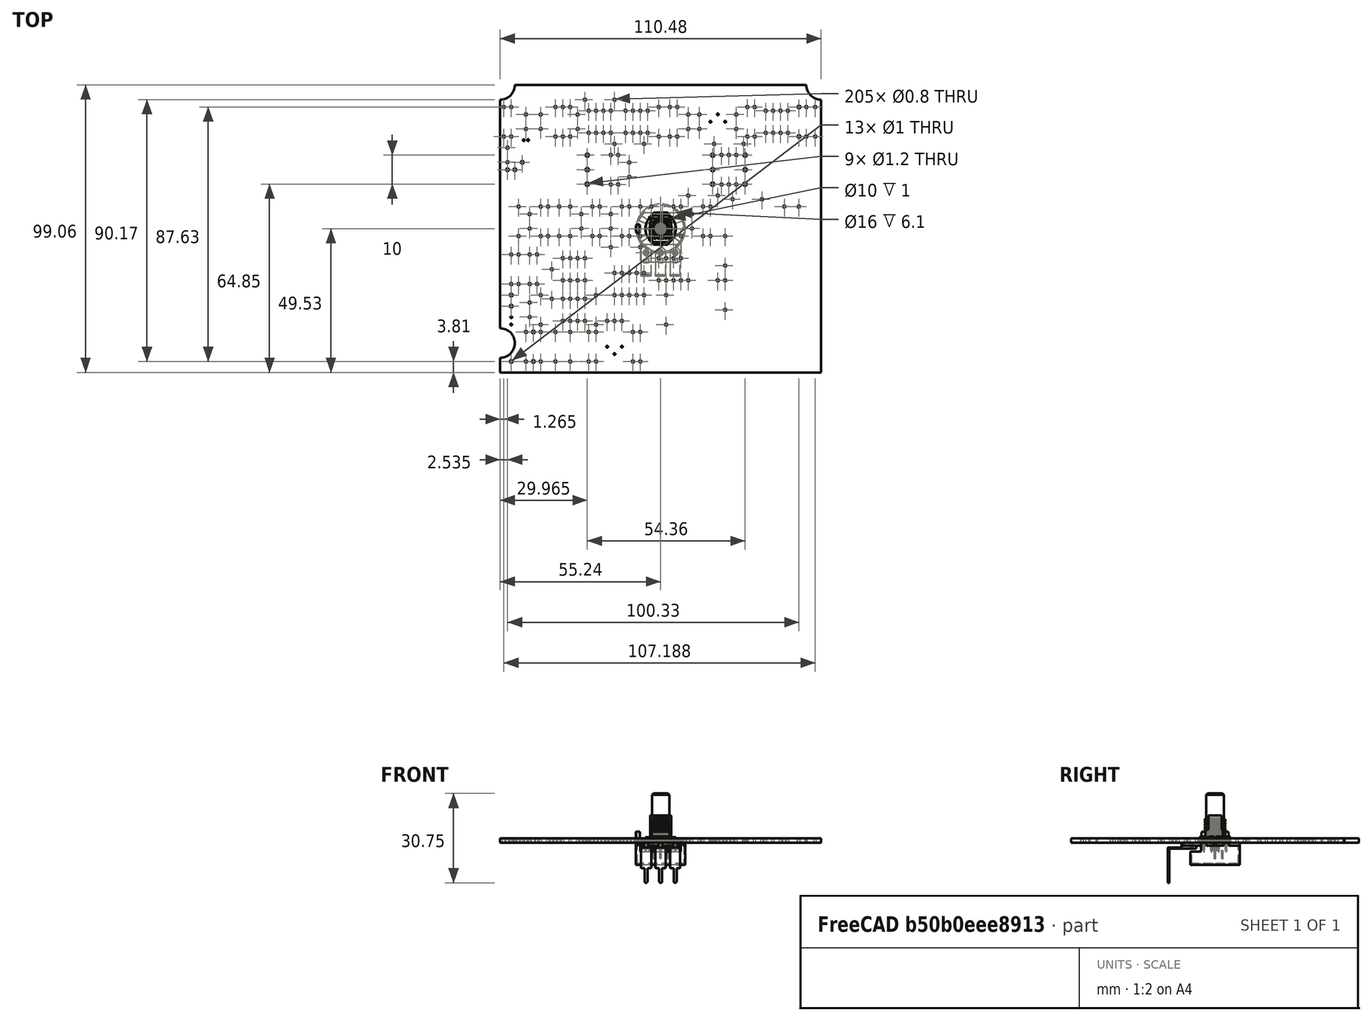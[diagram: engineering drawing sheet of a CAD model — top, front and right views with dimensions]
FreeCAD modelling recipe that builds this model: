
FCSTD DOCUMENT  (FreeCAD 0.19R17089 +1543 (Git))
Label: PRJ-003-#000-000 - Lid Assy
License: All rights reserved
LicenseURL: http://en.wikipedia.org/wiki/All_rights_reserved
objects: App::Link×58, Part::Feature×37, App::LinkGroup×33, Part::FeaturePython×26, App::FeaturePython×7
note: 62 computed .brp shape members not serialized (recipe doc carries the construction recipe); baked Part::Feature solids carry a one-line shape summary decoded from their .brp
EXTERNAL_REF file=../#700-000 - Enclosure/#710-000 - 1590DD.FCStd obj=Cut
EXTERNAL_REF file=../#700-000 - Enclosure/#710-000 - 1590DD.FCStd obj=Part__Feature

FEATURE [App::Link] Link
  LinkPlacement = pos=(6.90814,-46.0555,79.4472) rot=(0,1,0;3.14159rad)
  LinkedObject = -> <external ../#700-000 - Enclosure/#710-000 - 1590DD.FCStd>#Cut
  Placement = pos=(6.90814,-46.0555,79.4472) rot=(0,1,0;3.14159rad)
FEATURE [Part::Feature] Solid  label="SOLID"
  shape: bbox 10.96 x 2.55 x 5.125 mm, 27 faces (baked)
FEATURE [App::LinkGroup] LinkGroup  label="R_CC25_P10.16_H_27k"
  ElementList = -> [Solid]
  LinkMode = 0
  Placement = pos=(53.213,36.83,1.65) rot=(0,0,1;1.5708rad)
FEATURE [Part::Feature] Solid001  label="SOLID001"
  shape: bbox 10.96 x 2.55 x 5.125 mm, 27 faces (baked)
FEATURE [App::LinkGroup] LinkGroup001  label="R_CC25_P10.16_H_100k"
  ElementList = -> [Solid001]
  LinkMode = 0
  Placement = pos=(50.165,36.83,1.65) rot=(0,0,-1;1.5708rad)
FEATURE [Part::Feature] Solid002  label="SOLID002"
  shape: bbox 10.96 x 2.55 x 5.125 mm, 27 faces (baked)
FEATURE [App::LinkGroup] LinkGroup002  label="R_CC25_P10.16_H_220R"
  ElementList = -> [Solid002]
  LinkMode = 0
  Placement = pos=(-22.225,-40.64,1.65) rot=(0,0,-1;1.5708rad)
FEATURE [Part::Feature] Solid003  label="SOLID003"
  shape: bbox 10.96 x 2.55 x 5.125 mm, 27 faces (baked)
FEATURE [App::LinkGroup] LinkGroup003  label="R_CC25_P10.16_H_68k"
  ElementList = -> [Solid003]
  LinkMode = 0
  Placement = pos=(-41.275,-40.64,1.65) rot=(0,0,-1;1.5708rad)
FEATURE [Part::Feature] Solid004  label="SOLID004"
  shape: bbox 10.96 x 2.55 x 5.125 mm, 27 faces (baked)
FEATURE [App::LinkGroup] LinkGroup004  label="R_CC25_P10.16_H_220k"
  ElementList = -> [Solid004]
  LinkMode = 0
  Placement = pos=(-24.765,-40.64,1.65) rot=(0,0,-1;1.5708rad)
FEATURE [Part::Feature] Solid005  label="SOLID005"
  shape: bbox 10.96 x 2.55 x 5.125 mm, 27 faces (baked)
FEATURE [App::LinkGroup] LinkGroup005  label="R_CC25_P10.16_H_10k"
  ElementList = -> [Solid005]
  LinkMode = 0
  Placement = pos=(-36.195,-40.64,1.65) rot=(0,0,-1;1.5708rad)
FEATURE [Part::Feature] Solid006  label="SOLID006"
  shape: bbox 10.96 x 2.55 x 5.125 mm, 27 faces (baked)
FEATURE [App::LinkGroup] LinkGroup006  label="R_CC25_P10.16_H_3.3k"
  ElementList = -> [Solid006]
  LinkMode = 0
  Placement = pos=(-31.115,-40.64,1.65) rot=(0,0,-1;1.5708rad)
FEATURE [Part::Feature] Solid007  label="SOLID007"
  shape: bbox 10.96 x 2.55 x 5.125 mm, 27 faces (baked)
FEATURE [App::LinkGroup] LinkGroup007  label="R_CC25_P10.16_H_47k"
  ElementList = -> [Solid007]
  LinkMode = 0
  Placement = pos=(-9.525,-40.64,1.65) rot=(0,0,-1;1.5708rad)
FEATURE [Part::Feature] Solid008  label="SOLID008"
  shape: bbox 10.96 x 2.55 x 5.125 mm, 27 faces (baked)
FEATURE [App::LinkGroup] LinkGroup008  label="R_CC25_P10.16_H_82k"
  ElementList = -> [Solid008]
  LinkMode = 0
  Placement = pos=(-6.985,-40.64,1.65) rot=(0,0,-1;1.5708rad)
FEATURE [Part::Feature] Solid009  label="SOLID009"
  shape: bbox 10.96 x 2.55 x 5.125 mm, 27 faces (baked)
FEATURE [App::LinkGroup] LinkGroup009  label="R_CC25_P10.16_H_560R"
  ElementList = -> [Solid009]
  LinkMode = 0
  Placement = pos=(20.955,20.32,1.65) rot=(0,0,-1;1.5708rad)
FEATURE [App::Link] Link001  label="R_CC25_P10.16_H_27k001"
  LinkPlacement = pos=(26.035,20.32,1.65) rot=(0,0,-1;1.5708rad)
  LinkedObject = -> LinkGroup
  Placement = pos=(26.035,20.32,1.65) rot=(0,0,-1;1.5708rad)
FEATURE [Part::Feature] Solid010  label="SOLID010"
  shape: bbox 10.96 x 2.55 x 5.125 mm, 27 faces (baked)
FEATURE [App::LinkGroup] LinkGroup010  label="R_CC25_P10.16_H_82R"
  ElementList = -> [Solid010]
  LinkMode = 0
  Placement = pos=(23.495,20.32,1.65) rot=(0,0,-1;1.5708rad)
FEATURE [Part::Feature] Solid011  label="SOLID011"
  shape: bbox 10.96 x 2.55 x 5.125 mm, 27 faces (baked)
FEATURE [App::LinkGroup] LinkGroup011  label="R_CC25_P10.16_H_56k"
  ElementList = -> [Solid011]
  LinkMode = 0
  Placement = pos=(32.385,36.83,1.65) rot=(0,0,1;1.5708rad)
FEATURE [App::Link] Link002  label="R_CC25_P10.16_H_47k001"
  LinkPlacement = pos=(29.845,36.83,1.65) rot=(0,0,-1;1.5708rad)
  LinkedObject = -> LinkGroup007
  Placement = pos=(29.845,36.83,1.65) rot=(0,0,-1;1.5708rad)
FEATURE [App::Link] Link003  label="R_CC25_P10.16_H_560R001"
  LinkPlacement = pos=(-46.355,-40.64,1.65) rot=(0,0,-1;1.5708rad)
  LinkedObject = -> LinkGroup009
  Placement = pos=(-46.355,-40.64,1.65) rot=(0,0,-1;1.5708rad)
FEATURE [App::Link] Link004  label="R_CC25_P10.16_H_27k002"
  LinkPlacement = pos=(-41.275,-27.94,1.65) rot=(0,0,1;1.5708rad)
  LinkedObject = -> LinkGroup
  Placement = pos=(-41.275,-27.94,1.65) rot=(0,0,1;1.5708rad)
FEATURE [Part::Feature] Solid012  label="SOLID012"
  shape: bbox 10.96 x 2.55 x 5.125 mm, 27 faces (baked)
FEATURE [App::LinkGroup] LinkGroup012  label="R_CC25_P10.16_H_8.2k"
  ElementList = -> [Solid012]
  LinkMode = 0
  Placement = pos=(-48.895,-13.97,1.65) rot=(0,0,-1;1.5708rad)
FEATURE [App::Link] Link005  label="R_CC25_P10.16_H_10k001"
  LinkPlacement = pos=(-51.435,-13.97,1.65) rot=(0,0,1;1.5708rad)
  LinkedObject = -> LinkGroup005
  Placement = pos=(-51.435,-13.97,1.65) rot=(0,0,1;1.5708rad)
FEATURE [App::Link] Link006  label="R_CC25_P10.16_H_8.2k001"
  LinkPlacement = pos=(-45.085,-13.97,1.65) rot=(0,0,1;1.5708rad)
  LinkedObject = -> LinkGroup012
  Placement = pos=(-45.085,-13.97,1.65) rot=(0,0,1;1.5708rad)
FEATURE [App::Link] Link007  label="R_CC25_P10.16_H_10k002"
  LinkPlacement = pos=(-42.545,-13.97,1.65) rot=(0,0,1;1.5708rad)
  LinkedObject = -> LinkGroup005
  Placement = pos=(-42.545,-13.97,1.65) rot=(0,0,1;1.5708rad)
FEATURE [App::Link] Link008  label="R_CC25_P10.16_H_220k001"
  LinkPlacement = pos=(17.145,2.54,1.65) rot=(0,0,-1;1.5708rad)
  LinkedObject = -> LinkGroup004
  Placement = pos=(17.145,2.54,1.65) rot=(0,0,-1;1.5708rad)
FEATURE [Part::Feature] Solid013  label="SOLID013"
  shape: bbox 10.96 x 2.55 x 5.125 mm, 27 faces (baked)
FEATURE [App::LinkGroup] LinkGroup013  label="R_CC25_P10.16_H_4.7k"
  ElementList = -> [Solid013]
  LinkMode = 0
  Placement = pos=(5.715,36.83,1.65) rot=(0,0,1;1.5708rad)
FEATURE [App::Link] Link009  label="R_CC25_P10.16_H_4.7k001"
  LinkPlacement = pos=(3.175,36.83,1.65) rot=(0,0,-1;1.5708rad)
  LinkedObject = -> LinkGroup013
  Placement = pos=(3.175,36.83,1.65) rot=(0,0,-1;1.5708rad)
FEATURE [App::Link] Link010  label="R_CC25_P10.16_H_220k002"
  LinkPlacement = pos=(14.605,2.54,1.65) rot=(0,0,-1;1.5708rad)
  LinkedObject = -> LinkGroup004
  Placement = pos=(14.605,2.54,1.65) rot=(0,0,-1;1.5708rad)
FEATURE [App::Link] Link011  label="R_CC25_P10.16_H_4.7k002"
  LinkPlacement = pos=(-0.635,36.83,1.65) rot=(0,0,-1;1.5708rad)
  LinkedObject = -> LinkGroup013
  Placement = pos=(-0.635,36.83,1.65) rot=(0,0,-1;1.5708rad)
FEATURE [App::Link] Link012  label="R_CC25_P10.16_H_4.7k003"
  LinkPlacement = pos=(6.985,2.54,1.65) rot=(0,0,-1;1.5708rad)
  LinkedObject = -> LinkGroup013
  Placement = pos=(6.985,2.54,1.65) rot=(0,0,-1;1.5708rad)
FEATURE [App::Link] Link013  label="R_CC25_P10.16_H_220k003"
  LinkPlacement = pos=(4.445,2.54,1.65) rot=(0,0,1;1.5708rad)
  LinkedObject = -> LinkGroup004
  Placement = pos=(4.445,2.54,1.65) rot=(0,0,1;1.5708rad)
FEATURE [App::Link] Link014  label="R_CC25_P10.16_H_4.7k004"
  LinkPlacement = pos=(-3.175,2.54,1.65) rot=(0,0,-1;1.5708rad)
  LinkedObject = -> LinkGroup013
  Placement = pos=(-3.175,2.54,1.65) rot=(0,0,-1;1.5708rad)
FEATURE [App::Link] Link015  label="R_CC25_P10.16_H_4.7k005"
  LinkPlacement = pos=(-6.985,2.54,1.65) rot=(0,0,-1;1.5708rad)
  LinkedObject = -> LinkGroup013
  Placement = pos=(-6.985,2.54,1.65) rot=(0,0,-1;1.5708rad)
FEATURE [App::Link] Link016  label="R_CC25_P10.16_H_220k004"
  LinkPlacement = pos=(-13.335,2.54,1.65) rot=(0,0,1;1.5708rad)
  LinkedObject = -> LinkGroup004
  Placement = pos=(-13.335,2.54,1.65) rot=(0,0,1;1.5708rad)
FEATURE [App::Link] Link017  label="R_CC25_P10.16_H_4.7k006"
  LinkPlacement = pos=(-10.795,2.54,1.65) rot=(0,0,-1;1.5708rad)
  LinkedObject = -> LinkGroup013
  Placement = pos=(-10.795,2.54,1.65) rot=(0,0,-1;1.5708rad)
FEATURE [App::Link] Link018  label="R_CC25_P10.16_H_4.7k007"
  LinkPlacement = pos=(-20.955,2.54,1.65) rot=(0,0,-1;1.5708rad)
  LinkedObject = -> LinkGroup013
  Placement = pos=(-20.955,2.54,1.65) rot=(0,0,-1;1.5708rad)
FEATURE [App::Link] Link019  label="R_CC25_P10.16_H_220k005"
  LinkPlacement = pos=(-23.495,2.54,1.65) rot=(0,0,1;1.5708rad)
  LinkedObject = -> LinkGroup004
  Placement = pos=(-23.495,2.54,1.65) rot=(0,0,1;1.5708rad)
FEATURE [App::Link] Link020  label="R_CC25_P10.16_H_4.7k008"
  LinkPlacement = pos=(-31.115,2.54,1.65) rot=(0,0,-1;1.5708rad)
  LinkedObject = -> LinkGroup013
  Placement = pos=(-31.115,2.54,1.65) rot=(0,0,-1;1.5708rad)
FEATURE [App::Link] Link021  label="R_CC25_P10.16_H_4.7k009"
  LinkPlacement = pos=(-34.925,2.54,1.65) rot=(0,0,-1;1.5708rad)
  LinkedObject = -> LinkGroup013
  Placement = pos=(-34.925,2.54,1.65) rot=(0,0,-1;1.5708rad)
FEATURE [App::Link] Link022  label="R_CC25_P10.16_H_220k006"
  LinkPlacement = pos=(-48.895,2.54,1.65) rot=(0,0,1;1.5708rad)
  LinkedObject = -> LinkGroup004
  Placement = pos=(-48.895,2.54,1.65) rot=(0,0,1;1.5708rad)
FEATURE [App::Link] Link023  label="R_CC25_P10.16_H_4.7k010"
  LinkPlacement = pos=(-38.735,2.54,1.65) rot=(0,0,-1;1.5708rad)
  LinkedObject = -> LinkGroup013
  Placement = pos=(-38.735,2.54,1.65) rot=(0,0,-1;1.5708rad)
FEATURE [App::Link] Link024  label="R_CC25_P10.16_H_4.7k011"
  LinkPlacement = pos=(-41.275,2.54,1.65) rot=(0,0,1;1.5708rad)
  LinkedObject = -> LinkGroup013
  Placement = pos=(-41.275,2.54,1.65) rot=(0,0,1;1.5708rad)
FEATURE [App::Link] Link025  label="R_CC25_P10.16_H_8.2k002"
  LinkPlacement = pos=(-17.145,20.32,1.65) rot=(0,0,1;1.5708rad)
  LinkedObject = -> LinkGroup012
  Placement = pos=(-17.145,20.32,1.65) rot=(0,0,1;1.5708rad)
FEATURE [App::Link] Link026  label="R_CC25_P10.16_H_4.7k012"
  LinkPlacement = pos=(-14.605,20.32,1.65) rot=(0,0,-1;1.5708rad)
  LinkedObject = -> LinkGroup013
  Placement = pos=(-14.605,20.32,1.65) rot=(0,0,-1;1.5708rad)
FEATURE [App::Link] Link027  label="R_CC25_P10.16_H_4.7k013"
  LinkPlacement = pos=(-31.115,36.83,1.65) rot=(0,0,-1;1.5708rad)
  LinkedObject = -> LinkGroup013
  Placement = pos=(-31.115,36.83,1.65) rot=(0,0,-1;1.5708rad)
FEATURE [App::Link] Link028  label="R_CC25_P10.16_H_4.7k014"
  LinkPlacement = pos=(-33.655,36.83,1.65) rot=(0,0,-1;1.5708rad)
  LinkedObject = -> LinkGroup013
  Placement = pos=(-33.655,36.83,1.65) rot=(0,0,-1;1.5708rad)
FEATURE [Part::Feature] Solid014  label="SOLID014"
  shape: bbox 10.96 x 2.55 x 5.125 mm, 27 faces (baked)
FEATURE [App::LinkGroup] LinkGroup014  label="R_CC25_P10.16_H_390k"
  ElementList = -> [Solid014]
  LinkMode = 0
  Placement = pos=(-36.195,36.83,1.65) rot=(0,0,-1;1.5708rad)
FEATURE [Part::Feature] Solid015  label="SOLID015"
  shape: bbox 10.96 x 2.55 x 5.125 mm, 27 faces (baked)
FEATURE [App::LinkGroup] LinkGroup015  label="R_CC25_P10.16_H_3.9k"
  ElementList = -> [Solid015]
  LinkMode = 0
  Placement = pos=(-51.435,36.83,1.65) rot=(0,0,1;1.5708rad)
FEATURE [App::Link] Link029  label="R_CC25_P10.16_H_390k001"
  LinkPlacement = pos=(-53.975,36.83,1.65) rot=(0,0,-1;1.5708rad)
  LinkedObject = -> LinkGroup014
  Placement = pos=(-53.975,36.83,1.65) rot=(0,0,-1;1.5708rad)
FEATURE [Part::Feature] Solid016  label="SOLID016"
  shape: bbox 7.036 x 7.036 x 7.61 mm, 57 faces (baked)
FEATURE [App::LinkGroup] LinkGroup016  label="Nichicon_UMA_Straight_D6.5_H5_P2.5_d0.45_LL2.6"
  ElementList = -> [Solid016]
  LinkMode = 0
  Placement = pos=(-51.435,-31.75,1.65) rot=(0,0,1;3.14159rad)
FEATURE [Part::Feature] Solid017  label="SOLID017"
  shape: bbox 4.33 x 4.33 x 7.61 mm, 61 faces (baked)
FEATURE [App::LinkGroup] LinkGroup017  label="Nichicon_UMA_Straight_D4_H5_P1.5_d0.45_LL2.6"
  ElementList = -> [Solid017]
  LinkMode = 0
  Placement = pos=(-46.355,30.48,1.65) rot=(0,0,-1;1.5708rad)
FEATURE [Part::Feature] Solid018  label="SOLID018"
  shape: bbox 5.54 x 3.625 x 10.42 mm, 233 faces (baked)
FEATURE [App::LinkGroup] LinkGroup018  label="ON_Semi_2N3904TAR"
  ElementList = -> [Solid018]
  LinkMode = 0
  Placement = pos=(-15.875,-31.75,1.65) rot=(0,0,1;3.14159rad)
FEATURE [Part::Feature] Solid019  label="SOLID019"
  shape: bbox 6.706 x 7.036 x 10.16 mm, 550 faces (baked)
FEATURE [App::LinkGroup] LinkGroup019  label="Bourns_3362P-1-104"
  ElementList = -> [Solid019]
  LinkMode = 0
  Placement = pos=(-15.875,-40.64,1.65) rot=(0,0,1;3.14159rad)
FEATURE [App::Link] Link030  label="Bourns_3362P-1-105"
  LinkPlacement = pos=(19.685,36.83,1.65) rot=(0,0,1;0rad)
  LinkedObject = -> LinkGroup019
  Placement = pos=(19.685,36.83,1.65) rot=(0,0,1;0rad)
FEATURE [Part::Feature] Solid020  label="SOLID020"
  shape: bbox 10.96 x 2.5 x 5.1 mm, 11 faces (baked)
FEATURE [App::LinkGroup] LinkGroup020  label="R_CF25_P10.16_H"
  ElementList = -> [Solid020]
  LinkMode = 0
  Placement = pos=(22.225,-22.86,1.65) rot=(0,0,1;1.5708rad)
FEATURE [App::Link] Link031  label="R_CF25_P10.16_H001"
  LinkPlacement = pos=(29.845,10.16,1.65) rot=(0,0,1;3.14159rad)
  LinkedObject = -> LinkGroup020
  Placement = pos=(29.845,10.16,1.65) rot=(0,0,1;3.14159rad)
FEATURE [App::Link] Link032  label="R_CF25_P10.16_H002"
  LinkPlacement = pos=(14.605,11.43,1.65) rot=(0,0,1;3.14159rad)
  LinkedObject = -> LinkGroup020
  Placement = pos=(14.605,11.43,1.65) rot=(0,0,1;3.14159rad)
FEATURE [App::Link] Link033  label="R_CF25_P10.16_H003"
  LinkPlacement = pos=(22.225,-7.62,1.65) rot=(0,0,1;1.5708rad)
  LinkedObject = -> LinkGroup020
  Placement = pos=(22.225,-7.62,1.65) rot=(0,0,1;1.5708rad)
FEATURE [App::Link] Link034  label="R_CF25_P10.16_H004"
  LinkPlacement = pos=(14.605,-17.78,1.65) rot=(0,0,1;3.14159rad)
  LinkedObject = -> LinkGroup020
  Placement = pos=(14.605,-17.78,1.65) rot=(0,0,1;3.14159rad)
FEATURE [App::Link] Link035  label="R_CF25_P10.16_H005"
  LinkPlacement = pos=(1.905,-27.94,1.65) rot=(0,0,-1;1.5708rad)
  LinkedObject = -> LinkGroup020
  Placement = pos=(1.905,-27.94,1.65) rot=(0,0,-1;1.5708rad)
FEATURE [App::Link] Link036  label="R_CF25_P10.16_H006"
  LinkPlacement = pos=(-12.065,-6.35,1.65) rot=(0,0,1;3.14159rad)
  LinkedObject = -> LinkGroup020
  Placement = pos=(-12.065,-6.35,1.65) rot=(0,0,1;3.14159rad)
FEATURE [App::Link] Link037  label="R_CF25_P10.16_H007"
  LinkPlacement = pos=(-22.225,-27.94,1.65) rot=(0,0,1;1.5708rad)
  LinkedObject = -> LinkGroup020
  Placement = pos=(-22.225,-27.94,1.65) rot=(0,0,1;1.5708rad)
FEATURE [App::Link] Link038  label="R_CF25_P10.16_H008"
  LinkPlacement = pos=(-37.465,-19.05,1.65) rot=(0,0,1;1.5708rad)
  LinkedObject = -> LinkGroup020
  Placement = pos=(-37.465,-19.05,1.65) rot=(0,0,1;1.5708rad)
FEATURE [App::Link] Link039  label="R_CF25_P10.16_H009"
  LinkPlacement = pos=(23.495,29.21,1.65) rot=(0,0,1;0rad)
  LinkedObject = -> LinkGroup020
  Placement = pos=(23.495,29.21,1.65) rot=(0,0,1;0rad)
FEATURE [App::Link] Link040  label="R_CF25_P10.16_H010"
  LinkPlacement = pos=(-10.795,29.21,1.65) rot=(0,0,1;0rad)
  LinkedObject = -> LinkGroup020
  Placement = pos=(-10.795,29.21,1.65) rot=(0,0,1;0rad)
FEATURE [App::Link] Link041  label="R_CF25_P10.16_H011"
  LinkPlacement = pos=(-20.955,44.45,1.65) rot=(0,0,1;0rad)
  LinkedObject = -> LinkGroup020
  Placement = pos=(-20.955,44.45,1.65) rot=(0,0,1;0rad)
FEATURE [Part::Feature] Solid021  label="SOLID021"
  shape: bbox 7.87 x 9.59 x 7.1 mm, 280 faces (baked)
FEATURE [App::LinkGroup] LinkGroup021  label="Texas_Instruments_RC4558P"
  ElementList = -> [Solid021]
  LinkMode = 0
  Placement = pos=(-8.255,36.83,1.65) rot=(0,0,1;1.5708rad)
FEATURE [App::Link] Link042  label="Texas_Instruments_RC4558P001"
  LinkPlacement = pos=(3.175,-13.97,1.65) rot=(0,0,1;1.5708rad)
  LinkedObject = -> LinkGroup021
  Placement = pos=(3.175,-13.97,1.65) rot=(0,0,1;1.5708rad)
FEATURE [App::Link] Link043  label="Texas_Instruments_RC4558P002"
  LinkPlacement = pos=(-29.845,-13.97,1.65) rot=(0,0,1;1.5708rad)
  LinkedObject = -> LinkGroup021
  Placement = pos=(-29.845,-13.97,1.65) rot=(0,0,1;1.5708rad)
FEATURE [App::Link] Link044  label="Texas_Instruments_RC4558P003"
  LinkPlacement = pos=(40.005,36.83,1.65) rot=(0,0,1;1.5708rad)
  LinkedObject = -> LinkGroup021
  Placement = pos=(40.005,36.83,1.65) rot=(0,0,1;1.5708rad)
FEATURE [App::Link] Link045  label="Texas_Instruments_RC4558P004"
  LinkPlacement = pos=(-29.845,-27.94,1.65) rot=(0,0,1;1.5708rad)
  LinkedObject = -> LinkGroup021
  Placement = pos=(-29.845,-27.94,1.65) rot=(0,0,1;1.5708rad)
FEATURE [App::Link] Link046  label="Texas_Instruments_RC4558P005"
  LinkPlacement = pos=(-20.955,36.83,1.65) rot=(0,0,1;1.5708rad)
  LinkedObject = -> LinkGroup021
  Placement = pos=(-20.955,36.83,1.65) rot=(0,0,1;1.5708rad)
FEATURE [Part::Feature] Compound  label="COMPOUND"
  shape: bbox 13.5 x 9.75 x 13.95 mm, 243 faces, 3 solids (baked)
FEATURE [Part::Feature] Solid022  label="SOLID022"
  shape: bbox 6 x 6 x 8.5 mm, 4 faces (baked)
FEATURE [Part::Feature] Solid023  label="SOLID023"
  shape: bbox 7.238 x 7.394 x 6.855 mm, 40 faces (baked)
FEATURE [Part::Feature] Solid024  label="SOLID024"
  shape: bbox 16.98 x 20 x 1 mm, 46 faces (baked)
FEATURE [Part::Feature] Solid025  label="SOLID025"
  shape: bbox 17.02 x 17 x 11.4 mm, 108 faces (baked)
FEATURE [App::LinkGroup] LinkGroup022  label="RV16AF-41-15R"
  ElementList = -> [Compound,Solid022,Solid023,Solid024,Solid025]
  LinkMode = 0
  Placement = pos=(45.085,20.32,10.65) rot=(0,0,-1;1.5708rad)
FEATURE [App::Link] Link047  label="RV16AF-41-15R001"
  LinkPlacement = pos=(1.905,20.32,10.65) rot=(0,0,1;1.5708rad)
  LinkedObject = -> LinkGroup022
  Placement = pos=(1.905,20.32,10.65) rot=(0,0,1;1.5708rad)
FEATURE [App::Link] Link048  label="RV16AF-41-15R002"
  LinkPlacement = pos=(-41.275,20.32,10.65) rot=(0,0,1;1.5708rad)
  LinkedObject = -> LinkGroup022
  Placement = pos=(-41.275,20.32,10.65) rot=(0,0,1;1.5708rad)
FEATURE [Part::Feature] Solid026  label="SOLID026"
  shape: bbox 10.84 x 1.862 x 4.391 mm, 17 faces (baked)
FEATURE [App::LinkGroup] LinkGroup023  label="DO-35_P10.16"
  ElementList = -> [Solid026]
  LinkMode = 0
  Placement = pos=(-43.815,-40.64,1.65) rot=(0,0,1;1.5708rad)
FEATURE [App::Link] Link049  label="DO-35_P10.017"
  LinkPlacement = pos=(47.625,36.83,1.65) rot=(0,0,1;1.5708rad)
  LinkedObject = -> LinkGroup023
  Placement = pos=(47.625,36.83,1.65) rot=(0,0,1;1.5708rad)
FEATURE [Part::Feature] Solid027  label="SOLID027"
  shape: bbox 15.3 x 3.9 x 9.5 mm, 432 faces (baked)
FEATURE [App::LinkGroup] LinkGroup024  label="Wima_FKS2G016801B00KSSD"
  ElementList = -> [Solid027]
  LinkMode = 0
  Placement = pos=(45.085,7.62,1.65) rot=(0,0,1;3.14159rad)
FEATURE [Part::Feature] Solid028  label="SOLID028"
  shape: bbox 15.3 x 4.65 x 10.5 mm, 395 faces (baked)
FEATURE [App::LinkGroup] LinkGroup025  label="Wima_MKS2C034701C00KSSD"
  ElementList = -> [Solid028]
  LinkMode = 0
  Placement = pos=(26.035,36.83,1.65) rot=(0,0,-1;1.5708rad)
FEATURE [Part::Feature] Solid029  label="SOLID029"
  shape: bbox 15.3 x 6.15 x 8 mm, 402 faces (baked)
FEATURE [App::LinkGroup] LinkGroup026  label="Wima_FKP2J006801D00JSSD"
  ElementList = -> [Solid029]
  LinkMode = 0
  Placement = pos=(-45.085,-27.94,1.65) rot=(0,0,-1;1.5708rad)
FEATURE [App::Link] Link050  label="Wima_MKS2C034701C00KSSD001"
  LinkPlacement = pos=(13.335,36.83,1.65) rot=(0,0,1;1.5708rad)
  LinkedObject = -> LinkGroup025
  Placement = pos=(13.335,36.83,1.65) rot=(0,0,1;1.5708rad)
FEATURE [App::Link] Link051  label="Wima_FKS2G016801B00KSSD001"
  LinkPlacement = pos=(9.525,36.83,1.65) rot=(0,0,1;1.5708rad)
  LinkedObject = -> LinkGroup024
  Placement = pos=(9.525,36.83,1.65) rot=(0,0,1;1.5708rad)
FEATURE [App::Link] Link052  label="Wima_FKS2G016801B00KSSD002"
  LinkPlacement = pos=(10.795,2.54,1.65) rot=(0,0,1;1.5708rad)
  LinkedObject = -> LinkGroup024
  Placement = pos=(10.795,2.54,1.65) rot=(0,0,1;1.5708rad)
FEATURE [App::Link] Link053  label="Wima_FKS2G016801B00KSSD003"
  LinkPlacement = pos=(0.635,2.54,1.65) rot=(0,0,-1;1.5708rad)
  LinkedObject = -> LinkGroup024
  Placement = pos=(0.635,2.54,1.65) rot=(0,0,-1;1.5708rad)
FEATURE [App::Link] Link054  label="Wima_FKS2G016801B00KSSD004"
  LinkPlacement = pos=(-17.145,2.54,1.65) rot=(0,0,-1;1.5708rad)
  LinkedObject = -> LinkGroup024
  Placement = pos=(-17.145,2.54,1.65) rot=(0,0,-1;1.5708rad)
FEATURE [App::Link] Link055  label="Wima_FKS2G016801B00KSSD005"
  LinkPlacement = pos=(-27.305,2.54,1.65) rot=(0,0,-1;1.5708rad)
  LinkedObject = -> LinkGroup024
  Placement = pos=(-27.305,2.54,1.65) rot=(0,0,-1;1.5708rad)
FEATURE [App::Link] Link056  label="Wima_FKS2G016801B00KSSD006"
  LinkPlacement = pos=(-45.085,2.54,1.65) rot=(0,0,-1;1.5708rad)
  LinkedObject = -> LinkGroup024
  Placement = pos=(-45.085,2.54,1.65) rot=(0,0,-1;1.5708rad)
FEATURE [Part::Feature] Solid030  label="SOLID030"
  shape: bbox 15.3 x 3.15 x 8.5 mm, 428 faces (baked)
FEATURE [App::LinkGroup] LinkGroup027  label="Wima_FKS2G013301A00KSSD"
  ElementList = -> [Solid030]
  LinkMode = 0
  Placement = pos=(-10.795,20.32,1.65) rot=(0,0,-1;1.5708rad)
FEATURE [Part::Feature] Solid031  label="SOLID031"
  shape: bbox 15.3 x 3.15 x 8.5 mm, 398 faces (baked)
FEATURE [App::LinkGroup] LinkGroup028  label="Wima_FKS2G011001A00KSSD"
  ElementList = -> [Solid031]
  LinkMode = 0
  Placement = pos=(-28.575,36.83,1.65) rot=(0,0,1;1.5708rad)
FEATURE [Part::Feature] Solid032  label="SOLID032"
  shape: bbox 15.3 x 6.15 x 11.5 mm, 409 faces (baked)
FEATURE [App::LinkGroup] LinkGroup029  label="Wima_MKS2F031001E00KSSD"
  ElementList = -> [Solid032]
  LinkMode = 0
  Placement = pos=(-41.275,36.83,1.65) rot=(0,0,-1;1.5708rad)
FEATURE [Part::Feature] Solid033  label="SOLID033"
  shape: bbox 15.3 x 6.15 x 8 mm, 368 faces (baked)
FEATURE [App::LinkGroup] LinkGroup030  label="Wima_FKP2J001001D00JSSD"
  ElementList = -> [Solid033]
  LinkMode = 0
  Placement = pos=(-46.355,36.83,1.65) rot=(0,0,-1;1.5708rad)
FEATURE [Part::Feature] Solid034  label="SOLID034"
  shape: bbox 15.3 x 4.65 x 10.5 mm, 401 faces (baked)
FEATURE [App::LinkGroup] LinkGroup031  label="Wima_MKS2F024701C00KSSD"
  ElementList = -> [Solid034]
  LinkMode = 0
  Placement = pos=(-52.705,25.4,1.65) rot=(0,0,1;1.5708rad)
FEATURE [Part::Feature] Solid035  label="COMPOUND001"
  shape: bbox 110.5 x 99.06 x 1.6 mm, 248 faces (baked)
FEATURE [App::LinkGroup] LinkGroup032  label="Open CASCADE STEP translator 6.9 1"
  ElementList = -> [LinkGroup,LinkGroup001,LinkGroup002,LinkGroup003,LinkGroup004,LinkGroup005,LinkGroup006,LinkGroup007,LinkGroup008,LinkGroup009,Link001,LinkGroup010,LinkGroup011,Link002,Link003,Link004,LinkGroup012,Link005,Link006,Link007,Link008,LinkGroup013,Link009,Link010,Link011,Link012,Link013,Link014,Link015,Link016,Link017,Link018,Link019,Link020,Link021,Link022,Link023,Link024,Link025,Link026,Link027,+48 more]
  LinkMode = 0
  Placement = pos=(-14.3819,-68.9155,65.2972) rot=(0,0,-1;3.14159rad)
FEATURE [App::Link] Link057
  LinkPlacement = pos=(103.908,-46.0555,-38.6528) rot=(0,0,-1;1.5708rad)
  LinkedObject = -> <external ../#700-000 - Enclosure/#710-000 - 1590DD.FCStd>#Part__Feature
  Placement = pos=(103.908,-46.0555,-38.6528) rot=(0,0,-1;1.5708rad)
FEATURE [Part::FeaturePython] Parts  # WARN: FeaturePython — macro-defined, semantics opaque (R4)
  Group = -> [Link,LinkGroup032,Link057]
  GroupMode = 0
FEATURE [Part::FeaturePython] Assembly  # WARN: FeaturePython — macro-defined, semantics opaque (R4)
  AutoRelax = true
  BuildShape = 0
  Freeze = false
  Group = -> [Constraints,Elements,Parts]
  GroupMode = 1
  SolverType = 1
  Verbose = false
  _SolverType = 1
  _Version = 1
FEATURE [App::FeaturePython] Constraints  # WARN: FeaturePython — macro-defined, semantics opaque (R4)
  Group = -> [Constraint001,Constraint]
  GroupMode = 1
  _Version = 1
FEATURE [App::FeaturePython] Elements  # WARN: FeaturePython — macro-defined, semantics opaque (R4)
  Group = -> [_Element,_Element001,_Element002,_Element003,_Element004,_Element005,_Element006,_Element007,_Element008,_Element009,_Element010,_Element011,_Element012,_Element013,_Element014,_Element015,_Element016,_Element017,_Element018,_Element019,_Element020,_Element021,_Element022,_Element023]
  GroupMode = 1
FEATURE [Part::FeaturePython] _Element  # link proxy (typed FeaturePython)
  Detach = false
  LinkTransform = true
  LinkedObject = -> LinkGroup032 [LinkGroup022.Solid025.Face43]
  _Parent = -> Elements
FEATURE [Part::FeaturePython] _Element001  # link proxy (typed FeaturePython)
  Detach = false
  LinkTransform = true
  LinkedObject = -> Link [Face3]
  _Parent = -> Elements
FEATURE [Part::FeaturePython] _Element002  # link proxy (typed FeaturePython)
  Detach = false
  LinkTransform = true
  LinkedObject = -> Link [Edge108]
  _Parent = -> Elements
FEATURE [Part::FeaturePython] _Element003  # link proxy (typed FeaturePython)
  Detach = false
  LinkTransform = true
  LinkedObject = -> LinkGroup032 [LinkGroup022.Solid022.Face4]
  _Parent = -> Elements
FEATURE [Part::FeaturePython] _Element004  # link proxy (typed FeaturePython)
  Detach = false
  LinkTransform = true
  LinkedObject = -> LinkGroup032 [LinkGroup022.Solid022.Edge5]
  _Parent = -> Elements
FEATURE [Part::FeaturePython] _Element005  # link proxy (typed FeaturePython)
  Detach = false
  LinkTransform = true
  LinkedObject = -> Link [Edge110]
  _Parent = -> Elements
FEATURE [Part::FeaturePython] _Element006  # link proxy (typed FeaturePython)
  Detach = false
  LinkTransform = true
  LinkedObject = -> Link [Edge40]
  _Parent = -> Elements
FEATURE [Part::FeaturePython] _Element007  # link proxy (typed FeaturePython)
  Detach = false
  LinkTransform = true
  LinkedObject = -> LinkGroup032 [Link047.Solid022.Edge5]
  _Parent = -> Elements
FEATURE [Part::FeaturePython] _Element008  # link proxy (typed FeaturePython)
  Detach = false
  LinkTransform = true
  LinkedObject = -> Link [Edge38]
  _Parent = -> Elements
FEATURE [Part::FeaturePython] _Element009  # link proxy (typed FeaturePython)
  Detach = false
  LinkTransform = true
  LinkedObject = -> LinkGroup032 [Link048.Solid022.Edge5]
  _Parent = -> Elements
FEATURE [Part::FeaturePython] _Element010  # link proxy (typed FeaturePython)
  Detach = false
  LinkTransform = true
  LinkedObject = -> Link [Edge39]
  _Parent = -> Elements
FEATURE [Part::FeaturePython] _Element011  # link proxy (typed FeaturePython)
  Detach = false
  LinkTransform = true
  LinkedObject = -> LinkGroup032 [Link048.Solid022.Face1]
  _Parent = -> Elements
FEATURE [Part::FeaturePython] _Element012  # link proxy (typed FeaturePython)
  Detach = false
  LinkTransform = true
  LinkedObject = -> Link [Face38]
  _Parent = -> Elements
FEATURE [Part::FeaturePython] _Element013  # link proxy (typed FeaturePython)
  Detach = false
  LinkTransform = true
  LinkedObject = -> LinkGroup032 [Link048.Solid022.Edge3]
  _Parent = -> Elements
FEATURE [Part::FeaturePython] _Element014  # link proxy (typed FeaturePython)
  Detach = false
  LinkTransform = true
  LinkedObject = -> LinkGroup032 [Link048.Solid022.Face4]
  _Parent = -> Elements
FEATURE [Part::FeaturePython] _Element015  # link proxy (typed FeaturePython)
  Detach = false
  LinkTransform = true
  LinkedObject = -> LinkGroup032 [Link048.Solid023.Edge10]
  _Parent = -> Elements
FEATURE [Part::FeaturePython] _Element016  # link proxy (typed FeaturePython)
  Detach = false
  LinkTransform = true
  LinkedObject = -> LinkGroup032 [LinkGroup022.Solid023.Edge3]
  _Parent = -> Elements
FEATURE [Part::FeaturePython] _Element017  # link proxy (typed FeaturePython)
  Detach = false
  LinkTransform = true
  LinkedObject = -> Link [Edge702]
  _Parent = -> Elements
FEATURE [Part::FeaturePython] _Element018  # link proxy (typed FeaturePython)
  Detach = false
  LinkTransform = true
  LinkedObject = -> Link057 [Edge544]
  _Parent = -> Elements
FEATURE [Part::FeaturePython] _Element019  # link proxy (typed FeaturePython)
  Detach = false
  LinkTransform = true
  LinkedObject = -> Link [Edge700]
  _Parent = -> Elements
FEATURE [Part::FeaturePython] _Element020  # link proxy (typed FeaturePython)
  Detach = false
  LinkTransform = true
  LinkedObject = -> Link057 [Edge526]
  _Parent = -> Elements
FEATURE [Part::FeaturePython] _Element021  # link proxy (typed FeaturePython)
  Detach = false
  LinkTransform = true
  LinkedObject = -> LinkGroup032 [Link048.Solid023.Edge3]
  _Parent = -> Elements
FEATURE [Part::FeaturePython] _Element022  # link proxy (typed FeaturePython)
  Detach = false
  LinkTransform = true
  LinkedObject = -> LinkGroup032 [LinkGroup022.Solid022.Edge3]
  _Parent = -> Elements
FEATURE [App::FeaturePython] Constraint001  label="Attachment"  # WARN: FeaturePython — macro-defined, semantics opaque (R4)
  Cascade = false
  ConstraintType = 3
  Disabled = false
  Group = -> [ElementLink001,ElementLink002]
  GroupMode = 1
  Multiply = false
  _ConstraintType = 45
  _Parent = -> Constraints
FEATURE [App::FeaturePython] ElementLink001  label="_Element016"  # link proxy (typed FeaturePython)
  LinkTransform = true
  LinkedObject = -> _Element016
  _Parent = -> Constraint001
FEATURE [App::FeaturePython] ElementLink002  label="_Element006"  # link proxy (typed FeaturePython)
  LinkTransform = true
  LinkedObject = -> _Element006
  _Parent = -> Constraint001
FEATURE [Part::FeaturePython] _Element023  # link proxy (typed FeaturePython)
  Detach = false
  LinkTransform = true
  LinkedObject = -> Link [Face37]
  _Parent = -> Elements
FEATURE [App::FeaturePython] Constraint  label="Locked"  # WARN: FeaturePython — macro-defined, semantics opaque (R4)
  ConstraintType = 0
  Disabled = false
  Group = -> [ElementLink]
  GroupMode = 1
  _ConstraintType = 0
  _Parent = -> Constraints
FEATURE [App::FeaturePython] ElementLink  label="_Element001"  # link proxy (typed FeaturePython)
  LinkTransform = true
  LinkedObject = -> _Element001
  _Parent = -> Constraint
